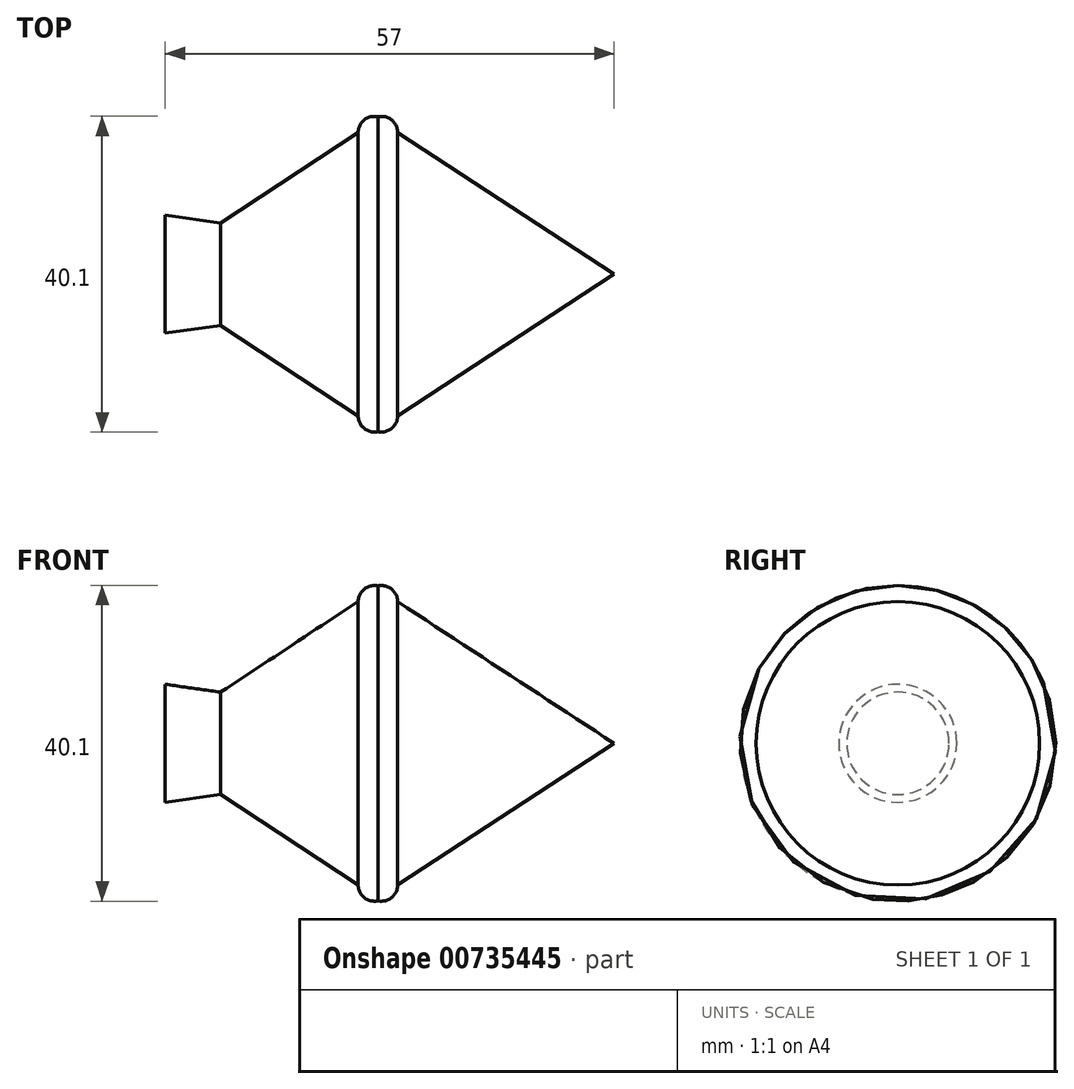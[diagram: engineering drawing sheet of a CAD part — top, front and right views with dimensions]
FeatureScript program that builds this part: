
annotation { "Feature Type Name" : "Feature", "Feature Type Description" : "" }
export const myFeature = defineFeature(function(context is Context, id is Id, definition is map)
    precondition{}
    {
        {
            var Q0;
            Q0=qCreatedBy(makeId("Top.planeOp"),FACE);
            var sketch = newSketch(context, id + "F0", { "sketchPlane" : qUnion([Q0])});
            skLineSegment(sketch, "E0", {"start": v(-20.04, 0.08) * mm, "end": v(19.96, 0.08) * mm});
            skLineSegment(sketch, "E1", {"start": v(-20.04, 0.08) * mm, "end": v(-27.04, 0.08) * mm});
            skLineSegment(sketch, "E2", {"start": v(-20.04, 0.08) * mm, "end": v(-20.04, 6.58) * mm});
            skLineSegment(sketch, "E3", {"start": v(-20.04, 6.58) * mm, "end": v(-27.04, 7.58) * mm});
            skLineSegment(sketch, "E4", {"start": v(-0.04, 0.08) * mm, "end": v(-0.04, 20.08) * mm});
            skLineSegment(sketch, "E5", {"start": v(19.96, 0.08) * mm, "end": v(29.96, 0.08) * mm});
            skLineSegment(sketch, "E6", {"start": v(29.96, 0.08) * mm, "end": v(2.46, 18.08) * mm});
            skLineSegment(sketch, "E7", {"start": v(-2.54, 18.08) * mm, "end": v(-20.04, 6.58) * mm});
            skLineSegment(sketch, "E8.MirrorCS", {"start": v(29.96, 0.08) * mm, "end": v(2.46, -17.92) * mm});
            skLineSegment(sketch, "E9.MirrorCS", {"start": v(-20.04, 0.08) * mm, "end": v(-20.04, -6.42) * mm});
            skLineSegment(sketch, "E10.MirrorCS", {"start": v(-20.04, -6.42) * mm, "end": v(-27.04, -7.42) * mm});
            skLineSegment(sketch, "E11.MirrorCS", {"start": v(-0.04, 0.08) * mm, "end": v(-0.04, -19.92) * mm});
            skLineSegment(sketch, "E12.MirrorCS", {"start": v(-2.54, -17.92) * mm, "end": v(-20.04, -6.42) * mm});
            skLineSegment(sketch, "E13", {"start": v(-2.54, 18.08) * mm, "end": v(-2.54, 0.08) * mm});
            skLineSegment(sketch, "E14", {"start": v(-2.54, 0.08) * mm, "end": v(-2.54, -17.92) * mm});
            skLineSegment(sketch, "E15", {"start": v(2.46, -17.92) * mm, "end": v(2.46, 0.08) * mm});
            skLineSegment(sketch, "E16", {"start": v(2.46, 0.08) * mm, "end": v(2.46, 18.08) * mm});
            skArc(sketch, "E17", {"start": v(-2.54, -17.92) * mm, "mid": v(-1.77, -19.52) * mm, "end": v(-0.04, -19.92) * mm});
            skArc(sketch, "E18", {"start": v(-0.04, -19.92) * mm, "mid": v(1.7, -19.52) * mm, "end": v(2.46, -17.92) * mm});
            skArc(sketch, "E19", {"start": v(-0.04, 20.08) * mm, "mid": v(-1.77, 19.68) * mm, "end": v(-2.54, 18.08) * mm});
            skArc(sketch, "E20", {"start": v(2.46, 18.08) * mm, "mid": v(1.7, 19.68) * mm, "end": v(-0.04, 20.08) * mm});
            skLineSegment(sketch, "E21", {"start": v(-27.04, 7.58) * mm, "end": v(-27.04, -7.42) * mm});
            skSolve(sketch);
        }
        {
            var Q0;
            Q0=makeQuery(id+"F0.imprint","IMPRINT",FACE,{"disambiguationData":[TD([[makeQuery(id+"F0.imprint","IMPRINT",EDGE,{"derivedFrom":sQuery(id+"F0.wireOp",EDGE,"E2")}),1.0]])]});
            var Q1;
            {var subQ0=sQuery(id+"F0.wireOp",EDGE,"E2");Q1=makeQuery(id+"F0.imprint","IMPRINT",FACE,{"disambiguationData":[TD([[makeQuery(id+"F0.imprint","IMPRINT",EDGE,{"derivedFrom":subQ0}),-1.0]])]});}
            var Q2;
            {var subQ0=sQuery(id+"F0.wireOp",EDGE,"E4");Q2=makeQuery(id+"F0.imprint","IMPRINT",FACE,{"disambiguationData":[TD([[makeQuery(id+"F0.imprint","IMPRINT",EDGE,{"derivedFrom":subQ0}),1.0]])]});}
            var Q3;
            {var subQ0=sQuery(id+"F0.wireOp",EDGE,"E4");Q3=makeQuery(id+"F0.imprint","IMPRINT",FACE,{"disambiguationData":[TD([[makeQuery(id+"F0.imprint","IMPRINT",EDGE,{"derivedFrom":subQ0}),-1.0]])]});}
            var Q4;
            Q4=makeQuery(id+"F0.imprint","IMPRINT",FACE,{"disambiguationData":[TD([[makeQuery(id+"F0.imprint","IMPRINT",EDGE,{"derivedFrom":sQuery(id+"F0.wireOp",EDGE,"E6")}),1.0]])]});
            var Q5;
            Q5=sQuery(id+"F0.wireOp",EDGE,"E0");
            revolve(context, id + "F1", {"surfaceOperationType" : NewSurfaceOperationType.NEW, "entities" : qUnion([Q0, Q1, Q2, Q3, Q4]), "axis" : qUnion([Q5]), "revolveType" : RevolveType.FULL});
        }
    });
